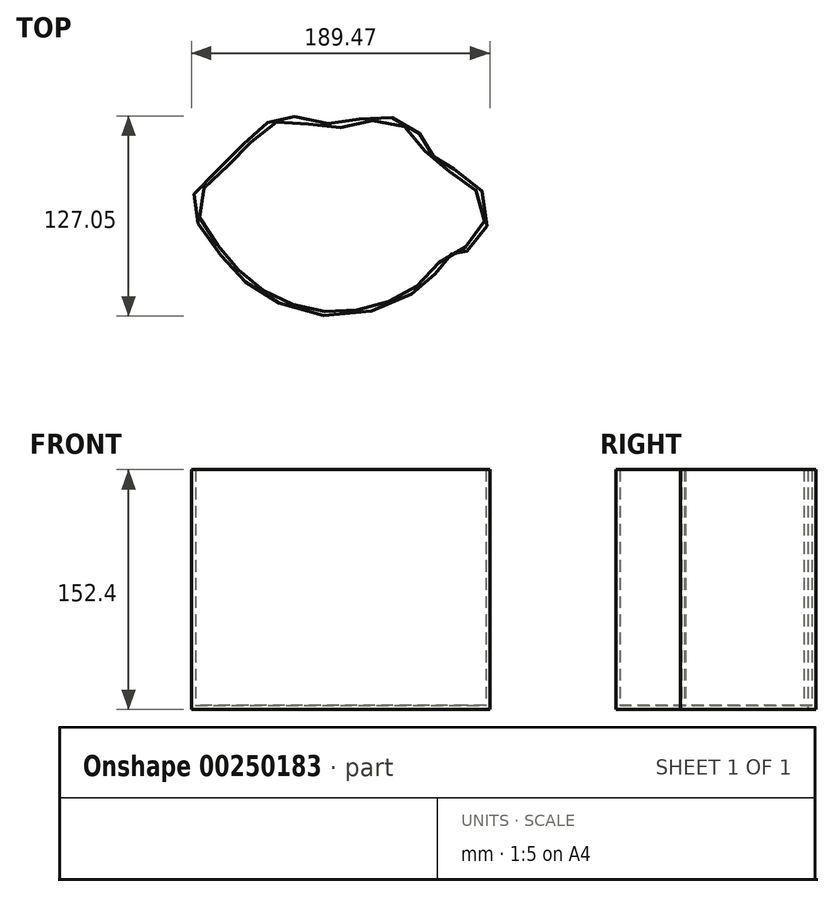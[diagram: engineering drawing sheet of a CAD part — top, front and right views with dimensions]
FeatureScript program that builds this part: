
annotation { "Feature Type Name" : "Feature", "Feature Type Description" : "" }
export const myFeature = defineFeature(function(context is Context, id is Id, definition is map)
    precondition{}
    {
        {
            var Q0;
            Q0=qCreatedBy(makeId("Top.planeOp"),FACE);
            var sketch = newSketch(context, id + "F0", { "sketchPlane" : qUnion([Q0])});
            skPoint(sketch, "E0.middle", {"position": v(2.65, 0) * mm});
            skPoint(sketch, "E1.visualSharp", {"position": v(-73.55, 50.8) * mm});
            skPoint(sketch, "E2.visualSharp", {"position": v(78.85, 50.8) * mm});
            skPoint(sketch, "E3.visualSharp", {"position": v(-73.55, -50.8) * mm});
            skPoint(sketch, "E4.visualSharp", {"position": v(78.85, -50.8) * mm});
            skFitSpline(sketch, "E5", {"points": [v(-73.55, 25.4) * mm, v(-48.15, 50.8) * mm, v(-29.01, 60.12) * mm, v(0, 55.14) * mm, v(27.12, 60.12) * mm, v(53.45, 50.8) * mm, v(64.17, 33.9) * mm, v(78.85, 25.4) * mm, v(99.71, 0) * mm, v(85.2, -25.47) * mm, v(78.85, -25.4) * mm, v(69.16, -34.79) * mm, v(53.45, -50.8) * mm, v(3.06, -66.86) * mm, v(-48.15, -50.8) * mm, v(-73.55, -25.4) * mm, v(-89.7, 5.52) * mm, v(-73.55, 25.4) * mm]});
            skSolve(sketch);
        }
        {
            var Q0;
            Q0=makeQuery(id+"F0.imprint","IMPRINT",FACE,{"disambiguationData":[TD([[makeQuery(id+"F0.imprint","IMPRINT",EDGE,{"derivedFrom":sQuery(id+"F0.wireOp",EDGE,"E5")}),-1.0]])]});
            extrude(context, id + "F1", {"entities" : qUnion([Q0]), "depth" : 152.4 * mm});
        }
        {
            var Q0;
            Q0=makeQuery(id+"F1.opExtrude","CAP_FACE",FACE,{"disambiguationData":[OSD([sQuery(id+"F0.wireOp",EDGE,"E5")])],"isStart":false});
            shell(context, id + "F2", {"entities" : qUnion([Q0]), "thickness" : 2.54 * mm});
        }
    });
